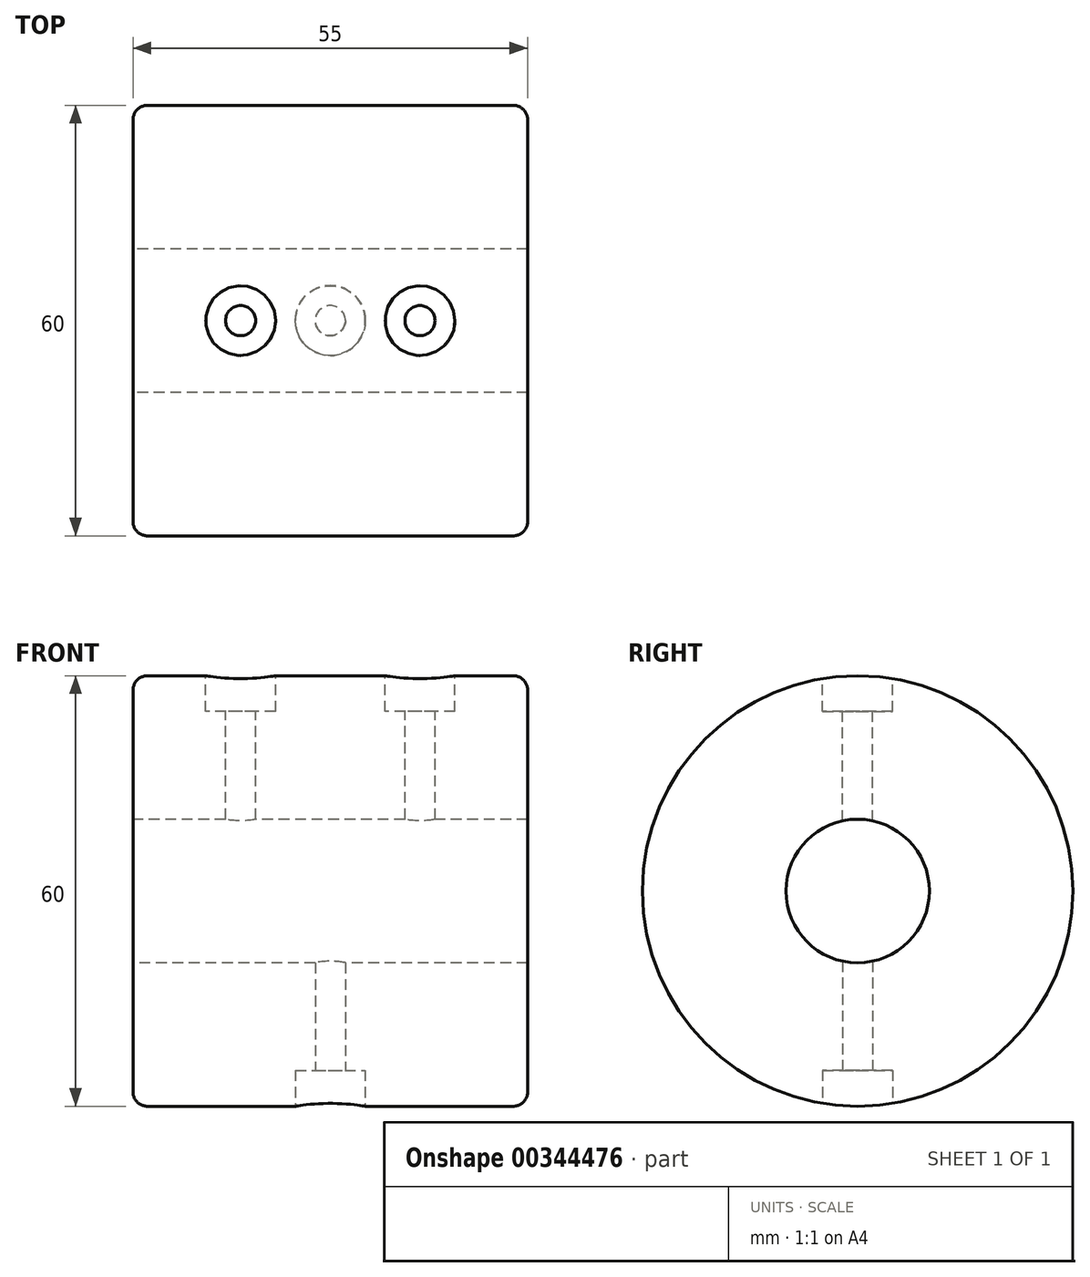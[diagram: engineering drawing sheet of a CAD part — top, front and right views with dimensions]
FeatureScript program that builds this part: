
annotation { "Feature Type Name" : "Feature", "Feature Type Description" : "" }
export const myFeature = defineFeature(function(context is Context, id is Id, definition is map)
    precondition{}
    {
        {
            var Q0;
            Q0=qCreatedBy(makeId("Top.planeOp"),FACE);
            cPlane(context, id + "F0", {"entities" : qUnion([Q0]), "cplaneType" : CPlaneType.OFFSET, "offset" : 30 * mm, "width" : 150 * mm, "height" : 150 * mm});
        }
        {
            var Q0;
            Q0=qCreatedBy(makeId("Top.planeOp"),FACE);
            cPlane(context, id + "F1", {"entities" : qUnion([Q0]), "cplaneType" : CPlaneType.OFFSET, "offset" : 30 * mm, "oppositeDirection" : true, "width" : 150 * mm, "height" : 150 * mm});
        }
        {
            var Q0;
            Q0=qCreatedBy(makeId("Right.planeOp"),FACE);
            var sketch = newSketch(context, id + "F2", { "sketchPlane" : qUnion([Q0])});
            skCircle(sketch, "E0", {"center": v(0, 0) * mm, "radius": 30 * mm});
            skCircle(sketch, "E1", {"center": v(0, 0) * mm, "radius": 10 * mm});
            skSolve(sketch);
        }
        {
            var Q0;
            Q0=qCreatedBy(id+"F0.planeOp",FACE);
            var sketch = newSketch(context, id + "F3", { "sketchPlane" : qUnion([Q0])});
            skPoint(sketch, "E2", {"position": v(-12.5, 0) * mm});
            skPoint(sketch, "E3", {"position": v(12.5, 0) * mm});
            skSolve(sketch);
        }
        {
            var Q0;
            Q0=qCreatedBy(id+"F1.planeOp",FACE);
            var sketch = newSketch(context, id + "F4", { "sketchPlane" : qUnion([Q0])});
            skPoint(sketch, "E4", {"position": v(0, 0) * mm});
            skSolve(sketch);
        }
        {
            var Q0;
            Q0 = qSketchRegion(id + "F2", true);
            extrude(context, id + "F5", {"entities" : qUnion([Q0]), "endBound" : BoundingType.SYMMETRIC, "depth" : 55 * mm});
        }
        {
            var Q0;
            Q0=makeQuery(id+"F5.opExtrude","CAP_EDGE",EDGE,{"disambiguationData":[OSD([sQuery(id+"F2.wireOp",EDGE,"E0")])],"isStart":false});
            var Q1;
            Q1=makeQuery(id+"F5.opExtrude","CAP_EDGE",EDGE,{"disambiguationData":[OSD([sQuery(id+"F2.wireOp",EDGE,"E0")])],"isStart":true});
            fillet(context, id + "F6", {"entities" : qUnion([Q0, Q1]), "radius" : 2 * mm, "tangentPropagation" : true, "allowEdgeOverflow" : false});
        }
        {
            var Q0;
            Q0=sQuery(id+"F3.wireOp",VERTEX,"E2");
            var Q1;
            Q1=sQuery(id+"F3.wireOp",VERTEX,"E3");
            var Q2;
            Q2=makeQuery(id+"F5.opExtrude","SWEPT_BODY",BODY,{"disambiguationData":[OSD([sQuery(id+"F2.wireOp",EDGE,"E0"),sQuery(id+"F2.wireOp",EDGE,"E1")])]});
            hole(context, id + "F7", {"style" : HoleStyle.C_BORE, "endStyle" : HoleEndStyle.BLIND, "standardTappedOrClearance" : lookupTablePath({ "standard" : "ISO", "engagement" : "75%", "pitch" : "0.8 mm", "size" : "M5", "type" : "Tapped" }), "standardBlindInLast" : lookupTablePath({ "standard" : "ISO", "engagement" : "75%", "pitch" : "0.8 mm", "size" : "M5", "type" : "Tapped" }), "holeDiameter" : 4.2 * mm, "cBoreDiameter" : 9.75 * mm, "cBoreDepth" : 5 * mm, "showTappedDepth" : true, "holeDepth" : 22 * mm, "isTappedThrough" : true, "tappedDepth" : 19.6 * mm, "tapClearance" : 3, "startFromSketch" : true, "locations" : qUnion([Q0, Q1]), "scope" : qUnion([Q2]), "majorDiameter" : 5 * mm});
        }
        {
            var Q0;
            Q0=sQuery(id+"F4.wireOp",VERTEX,"E4");
            var Q1;
            Q1=makeQuery(id+"F5.opExtrude","SWEPT_BODY",BODY,{"disambiguationData":[OSD([sQuery(id+"F2.wireOp",EDGE,"E0"),sQuery(id+"F2.wireOp",EDGE,"E1")])]});
            hole(context, id + "F8", {"style" : HoleStyle.C_BORE, "endStyle" : HoleEndStyle.BLIND, "oppositeDirection" : true, "standardTappedOrClearance" : lookupTablePath({ "standard" : "ISO", "engagement" : "75%", "pitch" : "0.8 mm", "size" : "M5", "type" : "Tapped" }), "standardBlindInLast" : lookupTablePath({ "standard" : "ISO", "engagement" : "75%", "pitch" : "0.8 mm", "size" : "M5", "type" : "Tapped" }), "holeDiameter" : 4.2 * mm, "cBoreDiameter" : 9.75 * mm, "cBoreDepth" : 5 * mm, "showTappedDepth" : true, "holeDepth" : 22 * mm, "isTappedThrough" : true, "tappedDepth" : 19.6 * mm, "tapClearance" : 3, "startFromSketch" : true, "locations" : qUnion([Q0]), "scope" : qUnion([Q1]), "majorDiameter" : 5 * mm});
        }
    });
